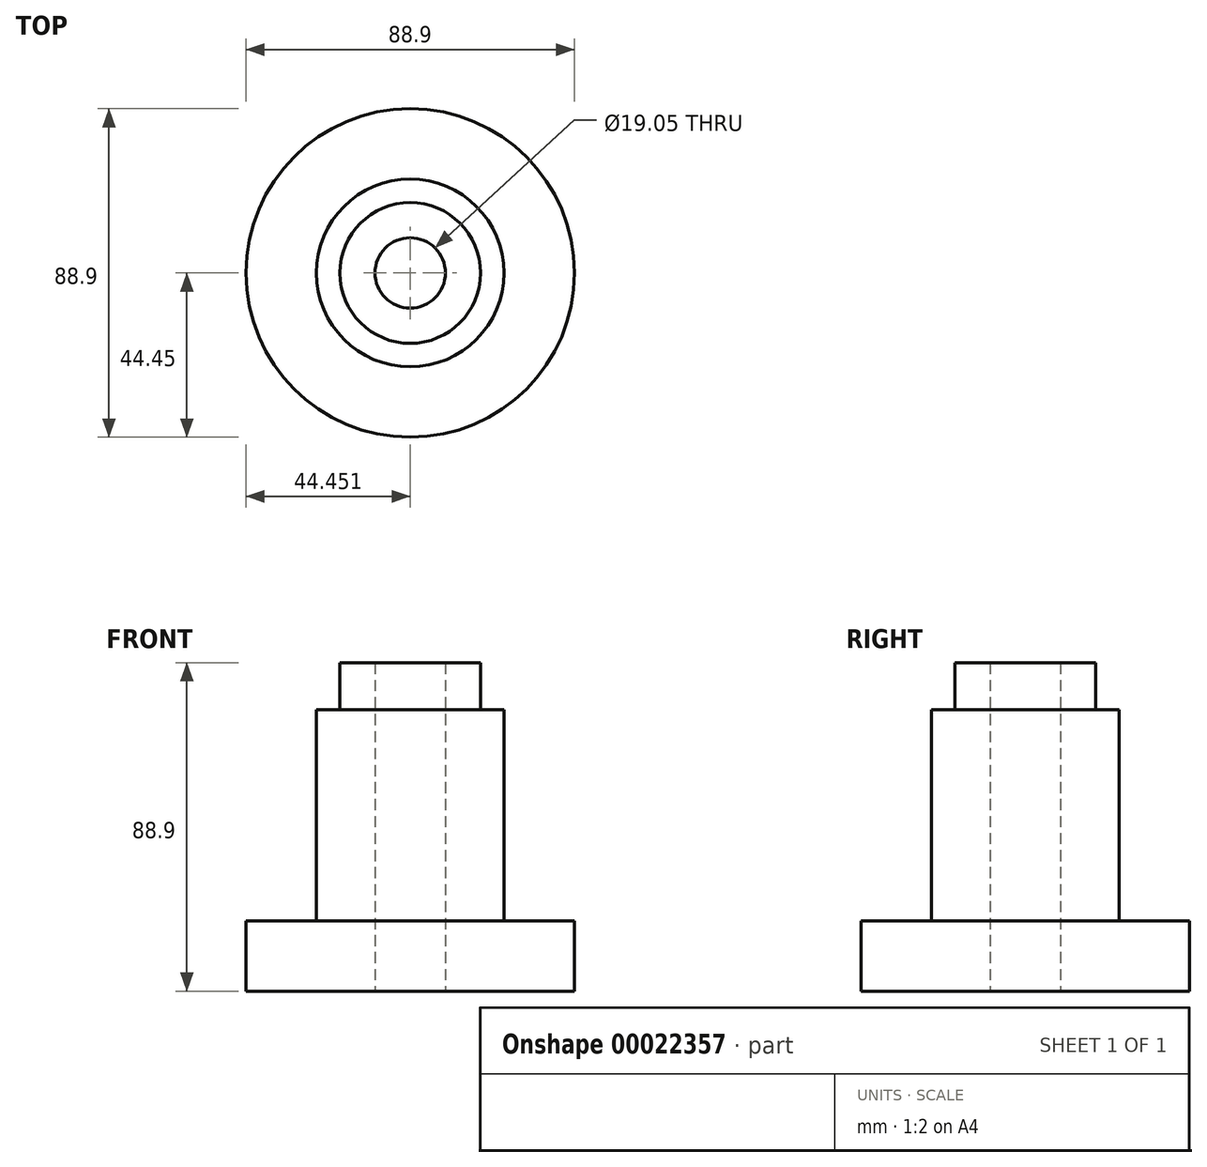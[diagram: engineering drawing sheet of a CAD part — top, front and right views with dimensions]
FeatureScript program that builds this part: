
annotation { "Feature Type Name" : "Feature", "Feature Type Description" : "" }
export const myFeature = defineFeature(function(context is Context, id is Id, definition is map)
    precondition{}
    {
        {
            var Q0;
            Q0=qCreatedBy(makeId("Front.planeOp"),FACE);
            var sketch = newSketch(context, id + "F0", { "sketchPlane" : qUnion([Q0])});
            skLineSegment(sketch, "E0", {"start": v(13.98, 50.45) * mm, "end": v(13.98, -38.18) * mm});
            skLineSegment(sketch, "E1", {"start": v(13.98, -38.18) * mm, "end": v(58.43, -38.18) * mm});
            skLineSegment(sketch, "E2", {"start": v(58.43, -38.18) * mm, "end": v(58.43, -19.13) * mm});
            skLineSegment(sketch, "E3", {"start": v(58.43, -19.13) * mm, "end": v(39.38, -19.13) * mm});
            skLineSegment(sketch, "E4", {"start": v(39.38, -19.13) * mm, "end": v(39.38, 38.02) * mm});
            skLineSegment(sketch, "E5", {"start": v(39.38, 38.02) * mm, "end": v(33.03, 38.02) * mm});
            skLineSegment(sketch, "E6", {"start": v(33.03, 38.02) * mm, "end": v(33.03, 50.72) * mm});
            skLineSegment(sketch, "E7", {"start": v(33.03, 50.72) * mm, "end": v(13.98, 50.45) * mm});
            skSolve(sketch);
        }
        {
            var Q0;
            Q0=makeQuery(id+"F0.imprint","IMPRINT",FACE,{"disambiguationData":[TD([[makeQuery(id+"F0.imprint","IMPRINT",EDGE,{"derivedFrom":sQuery(id+"F0.wireOp",EDGE,"E0")}),1.0]])]});
            var Q1;
            Q1=sQuery(id+"F0.wireOp",EDGE,"E0");
            revolve(context, id + "F1", {"entities" : qUnion([Q0]), "axis" : qUnion([Q1]), "revolveType" : RevolveType.FULL});
        }
        {
            var Q0;
            Q0=makeQuery(id+"F1.opRevolve","SWEPT_FACE",FACE,{"disambiguationData":[OSD([sQuery(id+"F0.wireOp",EDGE,"E1")])]});
            var sketch = newSketch(context, id + "F2", { "sketchPlane" : qUnion([Q0])});
            skCircle(sketch, "E8", {"center": v(13.98, 0) * mm, "radius": 9.53 * mm});
            skSolve(sketch);
        }
        {
            var Q0;
            Q0=makeQuery(id+"F2.imprint","IMPRINT",FACE,{"disambiguationData":[TD([[makeQuery(id+"F2.imprint","IMPRINT",EDGE,{"derivedFrom":sQuery(id+"F2.wireOp",EDGE,"E8")}),1.0]])]});
            extrude(context, id + "F3", {"entities" : qUnion([Q0]), "operationType" : NewBodyOperationType.REMOVE, "oppositeDirection" : true, "depth" : 101.6 * mm});
        }
    });
